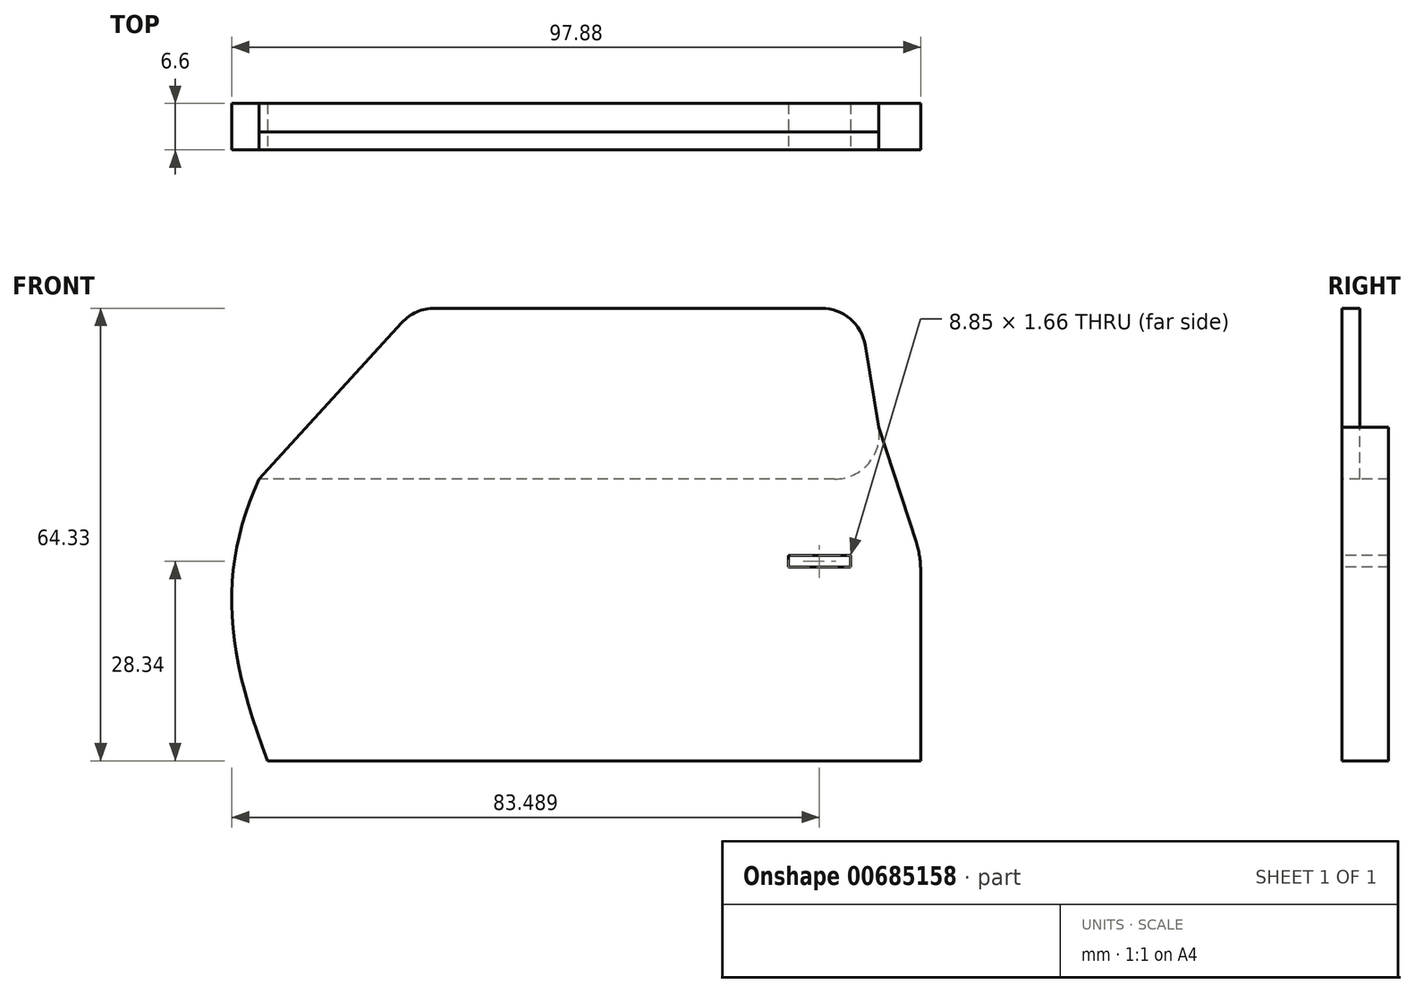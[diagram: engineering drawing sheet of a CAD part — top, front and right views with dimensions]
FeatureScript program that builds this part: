
annotation { "Feature Type Name" : "Feature", "Feature Type Description" : "" }
export const myFeature = defineFeature(function(context is Context, id is Id, definition is map)
    precondition{}
    {
        {
            var Q0;
            Q0=qCreatedBy(makeId("Front.planeOp"),FACE);
            var sketch = newSketch(context, id + "F0", { "sketchPlane" : qUnion([Q0])});
            skLineSegment(sketch, "E0.bottom", {"start": v(-66.07, -37.15) * mm, "end": v(26.68, -37.15) * mm});
            skLineSegment(sketch, "E0.top", {"start": v(-67.28, 2.9) * mm, "end": v(14.45, 2.9) * mm});
            skLineSegment(sketch, "E0.right", {"start": v(26.68, -37.15) * mm, "end": v(26.65, -10) * mm});
            skFitSpline(sketch, "E1", {"points": [v(-66.07, -37.15) * mm, v(-67.28, 2.9) * mm], "startDerivative": vector(-18.74, 48.67) * mm, "endDerivative": vector(17.18, 37.91) * mm});
            skLineSegment(sketch, "E2.bottom", {"start": v(7.86, -7.98) * mm, "end": v(16.71, -7.98) * mm});
            skLineSegment(sketch, "E2.top", {"start": v(7.86, -9.64) * mm, "end": v(16.71, -9.64) * mm});
            skLineSegment(sketch, "E2.left", {"start": v(7.86, -7.98) * mm, "end": v(7.86, -9.64) * mm});
            skLineSegment(sketch, "E2.right", {"start": v(16.71, -7.98) * mm, "end": v(16.71, -9.64) * mm});
            skLineSegment(sketch, "E3", {"start": v(-67.28, 2.9) * mm, "end": v(-47.03, 25.1) * mm});
            skPoint(sketch, "E4.visualSharp", {"position": v(-45.14, 27.18) * mm});
            skArc(sketch, "E4.filletArc", {"start": v(-42.34, 27.18) * mm, "mid": v(-44.9, 26.64) * mm, "end": v(-47.03, 25.1) * mm});
            skLineSegment(sketch, "E5", {"start": v(-42.34, 27.18) * mm, "end": v(12.53, 27.18) * mm});
            skLineSegment(sketch, "E6", {"start": v(18.8, 21.87) * mm, "end": v(20.71, 10.28) * mm});
            skPoint(sketch, "E7.visualSharp", {"position": v(17.91, 27.18) * mm});
            skArc(sketch, "E7.filletArc", {"start": v(18.8, 21.87) * mm, "mid": v(16.63, 25.67) * mm, "end": v(12.53, 27.18) * mm});
            skArc(sketch, "E8.filletArc", {"start": v(14.45, 2.9) * mm, "mid": v(19.3, 5.14) * mm, "end": v(20.71, 10.28) * mm});
            skLineSegment(sketch, "E9", {"start": v(20.71, 10.28) * mm, "end": v(26.03, -6.08) * mm});
            skArc(sketch, "E10.filletArc", {"start": v(26.65, -10) * mm, "mid": v(26.5, -8.02) * mm, "end": v(26.03, -6.08) * mm});
            skSolve(sketch);
        }
        {
            var Q0;
            Q0=makeQuery(id+"F0.imprint","IMPRINT",FACE,{"disambiguationData":[TD([[makeQuery(id+"F0.imprint","IMPRINT",EDGE,{"derivedFrom":sQuery(id+"F0.wireOp",EDGE,"E0.bottom")}),1.0]])]});
            extrude(context, id + "F1", {"entities" : qUnion([Q0]), "oppositeDirection" : true, "depth" : 6.6 * mm, "offsetDistance" : 25.4 * mm});
        }
        {
            var Q0;
            Q0 = qSketchRegion(id + "F0", true);
            extrude(context, id + "F2", {"entities" : qUnion([Q0]), "operationType" : NewBodyOperationType.ADD, "oppositeDirection" : true, "depth" : 2.54 * mm, "offsetDistance" : 25.4 * mm});
        }
    });
